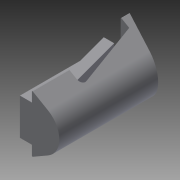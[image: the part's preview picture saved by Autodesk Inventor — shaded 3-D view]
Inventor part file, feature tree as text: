
AUTODESK INVENTOR PART (.ipt)
format: ipt  version: 2014 SP1 (Build 180222100, 222)  size: 181,248 bytes
history: native  units: in
note: dims shown in document units (in); Inventor stores cm internally (conversion verified against a paired STEP export)
features: extrude x7, sketch x5, projected_geometry x4, plane x3, mirror x2, fillet x1
ambient origin geometry x8: Origin, YZ Plane, XZ Plane, XY Plane, X Axis, Y Axis, Z Axis, Center Point
bodies: Solid1 (feature_tree)
feature tree (22):
  plane  "Work Plane1"
  plane  "Work Plane3"
  extrude  "Extrusion1"  Depth=1.0in TaperAngle=0.0deg
  plane  "Work Plane4"
  extrude  "Extrusion2"  Depth=0.1535in
  extrude  "Extrusion3"  Depth=0.036in
  extrude  "Extrusion4"  Depth=0.036in
  extrude  "Extrusion5"  Depth=0.1525in TaperAngle=0.0deg
  mirror  "Mirror1"
  extrude  "Extrusion6"  Depth=0.1525in TaperAngle=0.0deg
  mirror  "Mirror2"
  extrude  "Extrusion7"  Depth=0.1525in TaperAngle=0.0deg
  fillet  "Fillet1"  Radius=0.1525in
  sketch  "Sketch1"  dims[d0=1.0in d1=0.0in d2=1.0in d3=0.0in]
  sketch  "Sketch2"  dims[d4=0.042in d8=0.1535in]
  sketch  "Sketch6"  dims[d9=0.042in d10=0.036in]
  projected_geometry  "Projected Loop1"
  sketch  "Sketch7"  dims[d11=0.036in d12=0.028in]
  projected_geometry  "Projected Loop2"
  sketch  "Sketch8"  dims[d14=0.1525in d15=0.0in d16=0.1525in d17=0.0in d18=0.1525in d19=0.0in d20=0.1525in d21=0.0in d22=0.1525in d23=0.0in d24=0.0025in]
  projected_geometry  "Projected Loop3"
  projected_geometry  "Project Cut Edges1"
